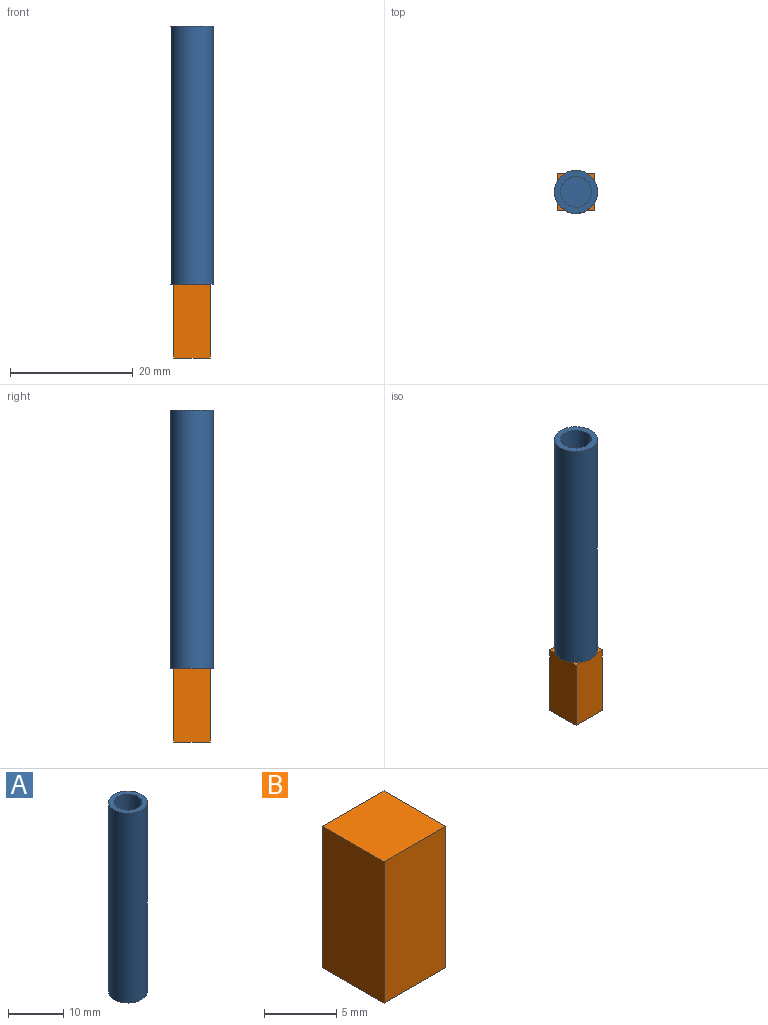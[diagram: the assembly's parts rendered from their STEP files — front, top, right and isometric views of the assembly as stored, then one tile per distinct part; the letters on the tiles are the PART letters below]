
ASSEMBLY  parts=2 mates=1
PART A: 5 faces, bbox 7x7x42 mm
  f0: cylinder r=2.5mm len=8mm, axis (0,0,-1), area 125.7mm2, adj f2,f3
  f1: cylinder r=3.5mm len=42mm, axis (0,0,-1), area 923.6mm2, adj f2,f4
  f2: plane 7x7mm, normal (0,0,1), area 18.8mm2, adj f0,f1
  f3: plane 5x5mm, normal (0,0,1), area 19.6mm2, adj f0
  f4: plane 7x7mm, normal (0,0,-1), area 38.5mm2, adj f1
PART B: 6 faces, bbox 6x6x12 mm
  f0: plane 12x6mm, normal (0,-1,0), area 72mm2, adj f1,f3,f4,f5
  f1: plane 12x6mm, normal (1,0,0), area 72mm2, adj f0,f2,f4,f5
  f2: plane 12x6mm, normal (0,1,0), area 72mm2, adj f1,f3,f4,f5
  f3: plane 12x6mm, normal (-1,0,0), area 72mm2, adj f0,f2,f4,f5
  f4: plane 6x6mm, normal (0,0,1), area 36mm2, adj f0,f1,f2,f3
  f5: plane 6x6mm, normal (0,0,-1), area 36mm2, adj f0,f1,f2,f3
PLACE A t=(-14.79,1.41,24.62)mm
PLACE B rot(axis=(1,0,0),180deg) t=(-14.79,1.41,-9.38)mm
MATE fastened B.f5 <-> A.f1  axis (0,0,1) through (-14.79,1.41,-9.38)mm
